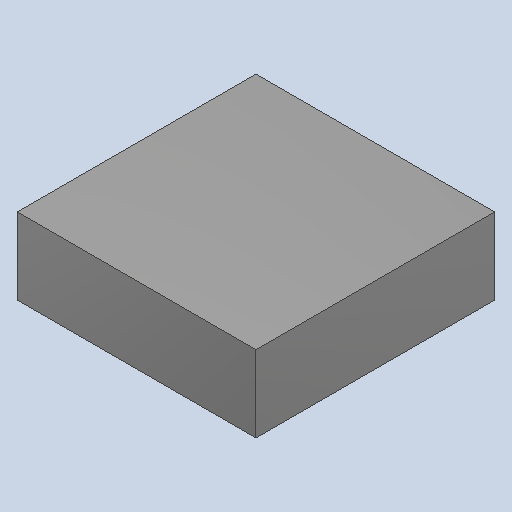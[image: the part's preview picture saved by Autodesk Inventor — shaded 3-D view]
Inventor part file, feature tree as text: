
AUTODESK INVENTOR PART (.ipt)
format: ipt  version: 2022.1 (Build 261234000, 234)  size: 85,504 bytes
history: imported  units: mm
features: imported_body x1
ambient origin geometry x8: Origin, YZ Plane, XZ Plane, XY Plane, X Axis, Y Axis, Z Axis, Center Point
bodies: Solid1 (imported_parasolid)
feature tree (1):
  imported_body  NMx_Import_Brep_tag  [imported B-rep: ~6 faces, bbox_mm=[2.5, 0.8, 2.5]]
